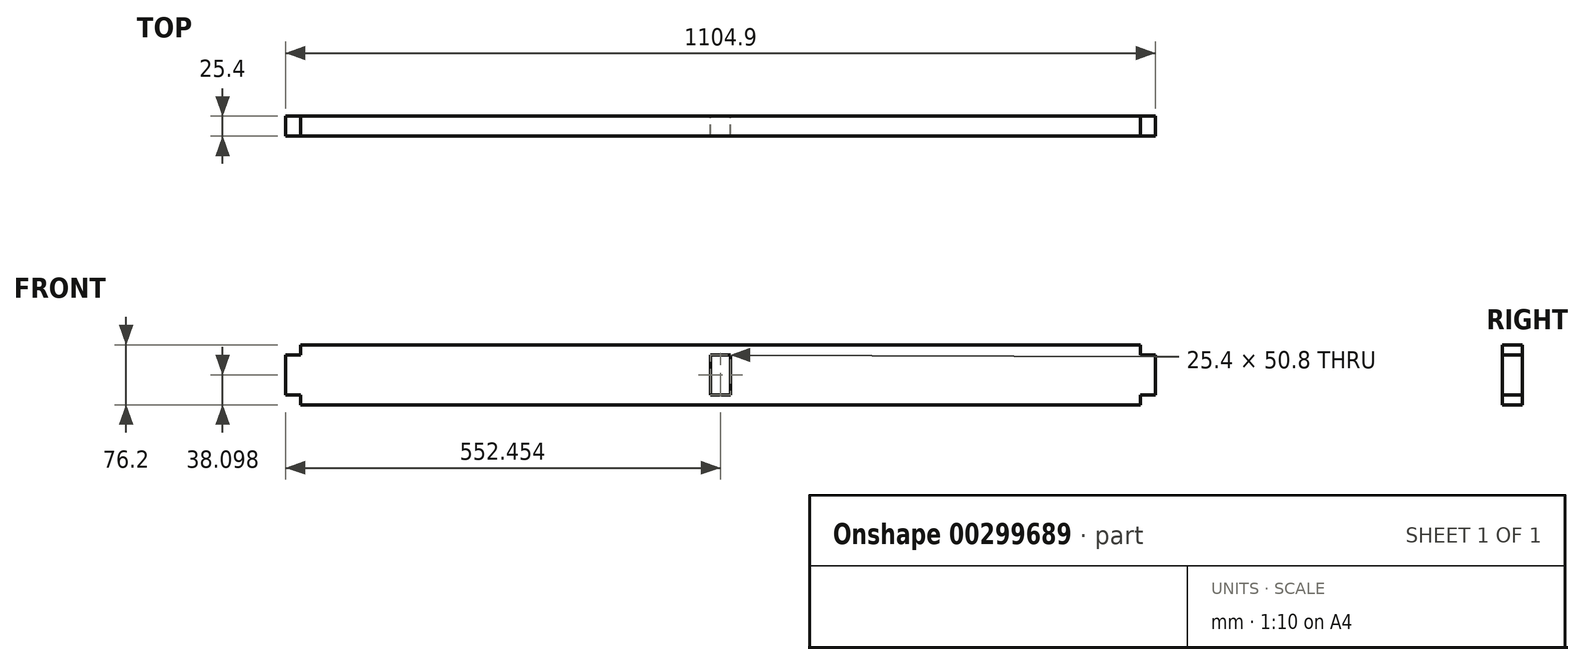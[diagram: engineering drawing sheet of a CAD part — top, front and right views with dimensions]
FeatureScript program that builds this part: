
annotation { "Feature Type Name" : "Feature", "Feature Type Description" : "" }
export const myFeature = defineFeature(function(context is Context, id is Id, definition is map)
    precondition{}
    {
        {
            var Q0;
            Q0=qCreatedBy(makeId("Front.planeOp"),FACE);
            var sketch = newSketch(context, id + "F0", { "sketchPlane" : qUnion([Q0])});
            skLineSegment(sketch, "E0.bottom", {"start": v(-128.95, 37.8) * mm, "end": v(937.85, 37.8) * mm});
            skLineSegment(sketch, "E0.top", {"start": v(-128.95, -38.4) * mm, "end": v(937.85, -38.4) * mm});
            skLineSegment(sketch, "E0.left", {"start": v(-128.95, 37.8) * mm, "end": v(-128.95, -38.4) * mm});
            skLineSegment(sketch, "E0.right", {"start": v(937.85, 37.8) * mm, "end": v(937.85, -38.4) * mm});
            skLineSegment(sketch, "E1.bottom", {"start": v(937.85, -25.7) * mm, "end": v(956.9, -25.7) * mm});
            skLineSegment(sketch, "E1.top", {"start": v(937.85, 25.1) * mm, "end": v(956.9, 25.1) * mm});
            skLineSegment(sketch, "E1.left", {"start": v(937.85, -25.7) * mm, "end": v(937.85, 25.1) * mm});
            skLineSegment(sketch, "E1.right", {"start": v(956.9, -25.7) * mm, "end": v(956.9, 25.1) * mm});
            skLineSegment(sketch, "E2.bottom", {"start": v(-128.95, 25.1) * mm, "end": v(-148, 25.1) * mm});
            skLineSegment(sketch, "E2.top", {"start": v(-128.95, -25.7) * mm, "end": v(-148, -25.7) * mm});
            skLineSegment(sketch, "E2.left", {"start": v(-128.95, 25.1) * mm, "end": v(-128.95, -25.7) * mm});
            skLineSegment(sketch, "E2.right", {"start": v(-148, 25.1) * mm, "end": v(-148, -25.7) * mm});
            skLineSegment(sketch, "E3.bottom", {"start": v(391.75, 25.1) * mm, "end": v(417.15, 25.1) * mm});
            skLineSegment(sketch, "E3.top", {"start": v(391.75, -25.7) * mm, "end": v(417.15, -25.7) * mm});
            skLineSegment(sketch, "E3.left", {"start": v(417.15, 25.1) * mm, "end": v(417.15, -25.7) * mm});
            skLineSegment(sketch, "E3.right", {"start": v(391.75, 25.1) * mm, "end": v(391.75, -25.7) * mm});
            skSolve(sketch);
        }
        {
            var Q0;
            Q0=qSketchRegion(id+"F0",true);
            extrude(context, id + "F1", {"entities" : qUnion([Q0]), "depth" : 25.4 * mm});
        }
    });
